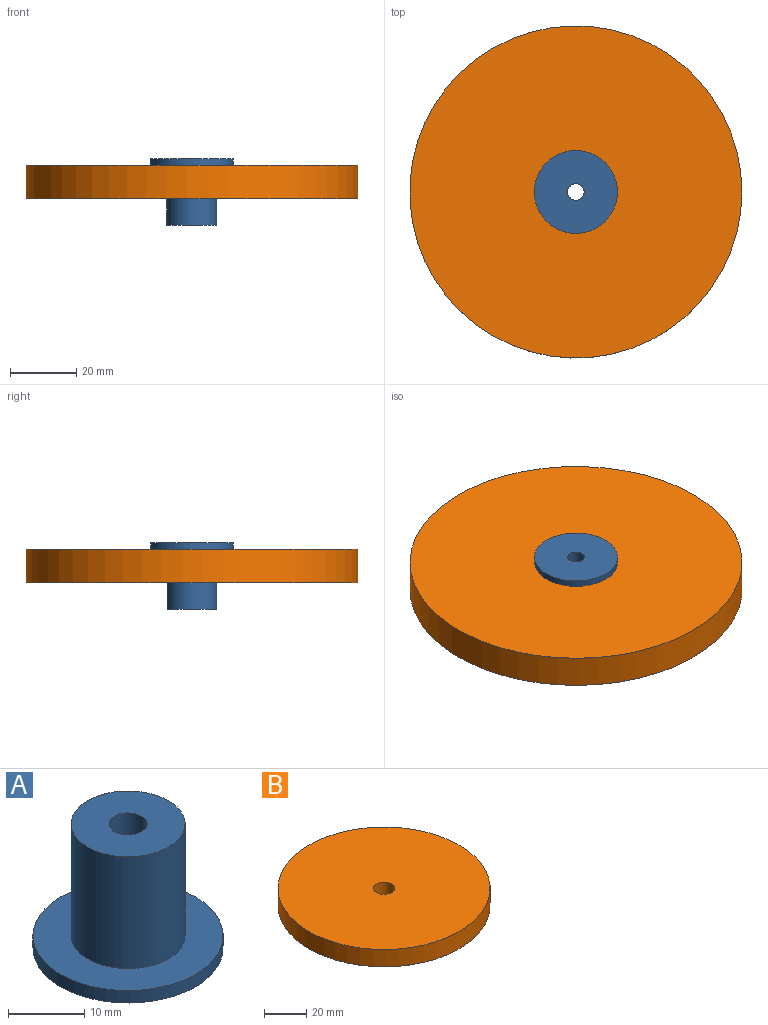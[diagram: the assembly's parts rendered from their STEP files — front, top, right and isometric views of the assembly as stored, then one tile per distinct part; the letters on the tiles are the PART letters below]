
ASSEMBLY  parts=2 mates=1
PART A: 6 faces, bbox 25x25x20 mm
  f0: cylinder r=12.5mm len=25mm, axis (0,0,-1), area 157.1mm2, adj f1,f2
  f1: plane 25x25mm, normal (0,0,1), area 314.2mm2, adj f0,f4
  f2: plane 25x25mm, normal (0,0,-1), area 471.2mm2, adj f0,f3
  f3: cylinder r=2.5mm len=20mm, axis (0,0,-1), area 314.2mm2, adj f2,f5
  f4: cylinder r=7.5mm len=18mm, axis (0,0,-1), area 848.2mm2, adj f1,f5
  f5: plane 15x15mm, normal (0,0,1), area 157.1mm2, adj f3,f4
PART B: 4 faces, bbox 100x100x10 mm
  f0: cylinder r=5mm len=10mm, axis (0,0,-1), area 314.2mm2, adj f2,f3
  f1: cylinder r=50mm len=100mm, axis (0,0,-1), area 3141.6mm2, adj f2,f3
  f2: plane 100x100mm, normal (0,0,1), area 7775.4mm2, adj f0,f1
  f3: plane 100x100mm, normal (0,0,-1), area 7775.4mm2, adj f0,f1
PLACE A rot(axis=(1,0,0),180deg) t=(-111.83,-31.55,56.53)mm
PLACE B t=(-111.83,-31.55,44.53)mm
MATE revolute A.f4 <-> B.f1  axis (0,0,1) through (-111.83,-31.55,54.53)mm
